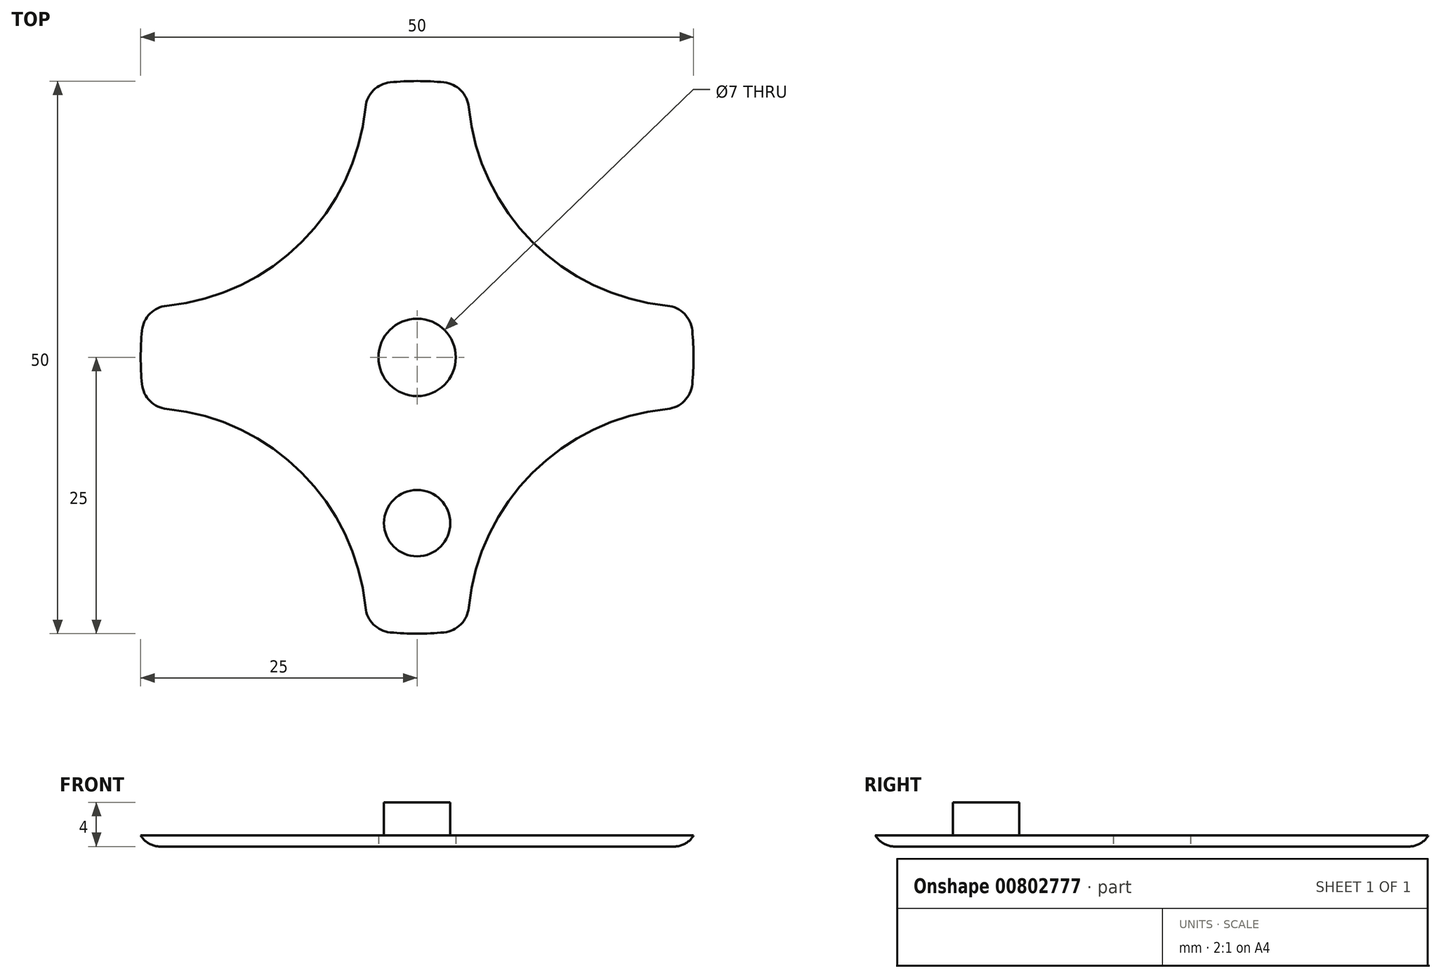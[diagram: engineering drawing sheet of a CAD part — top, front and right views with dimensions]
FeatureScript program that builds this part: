
annotation { "Feature Type Name" : "Feature", "Feature Type Description" : "" }
export const myFeature = defineFeature(function(context is Context, id is Id, definition is map)
    precondition{}
    {
        {
            var Q0;
            Q0=qCreatedBy(makeId("Top.planeOp"),FACE);
            var sketch = newSketch(context, id + "F0", { "sketchPlane" : qUnion([Q0])});
            skPoint(sketch, "E0.middle", {"position": v(0, 0) * mm});
            skArc(sketch, "E1", {"start": v(-24.58, 4.58) * mm, "mid": v(-25, 0) * mm, "end": v(-24.58, -4.58) * mm});
            skArc(sketch, "E2", {"start": v(-24.58, 4.58) * mm, "mid": v(-10.44, 10.44) * mm, "end": v(-4.58, 24.58) * mm});
            skLineSegment(sketch, "E3", {"start": v(0, 0) * mm, "end": v(-22.22, 22.22) * mm, "construction": true});
            skLineSegment(sketch, "E4", {"start": v(-4.58, 85.03) * mm, "end": v(-4.58, 7.7) * mm});
            skArc(sketch, "E5.1.0", {"start": v(-4.58, -24.58) * mm, "mid": v(-10.44, -10.44) * mm, "end": v(-24.58, -4.58) * mm});
            skArc(sketch, "E5.2.0", {"start": v(24.58, -4.58) * mm, "mid": v(10.44, -10.44) * mm, "end": v(4.58, -24.58) * mm});
            skArc(sketch, "E5.3.0", {"start": v(4.58, 24.58) * mm, "mid": v(10.44, 10.44) * mm, "end": v(24.58, 4.58) * mm});
            skArc(sketch, "E6.trimOffspring", {"start": v(4.58, 24.58) * mm, "mid": v(0, 25) * mm, "end": v(-4.58, 24.58) * mm});
            skArc(sketch, "E7.trimOffspring", {"start": v(24.58, -4.58) * mm, "mid": v(25, 0) * mm, "end": v(24.58, 4.58) * mm});
            skArc(sketch, "E8.trimOffspring", {"start": v(-4.58, -24.58) * mm, "mid": v(0, -25) * mm, "end": v(4.58, -24.58) * mm});
            skCircle(sketch, "E9", {"center": v(0, 0) * mm, "radius": 3.5 * mm});
            skSolve(sketch);
        }
        {
            var Q0;
            Q0=makeQuery(id+"F0.imprint","IMPRINT",FACE,{"disambiguationData":[TD([[makeQuery(id+"F0.imprint","IMPRINT",EDGE,{"derivedFrom":sQuery(id+"F0.wireOp",EDGE,"E0.bottom")}),1.0]])]});
            var Q1;
            Q1=makeQuery(id+"F0.imprint","IMPRINT",FACE,{"disambiguationData":[TD([[makeQuery(id+"F0.imprint","IMPRINT",EDGE,{"derivedFrom":sQuery(id+"F0.wireOp",EDGE,"E1")}),1.0]])]});
            extrude(context, id + "F1", {"entities" : qUnion([Q0, Q1]), "depth" : 4 * mm, "offsetDistance" : 25 * mm});
        }
        {
            var Q0;
            Q0=makeQuery(id+"F1.opExtrude","SWEPT_EDGE",EDGE,{"disambiguationData":[OSD([sQuery(id+"F0.wireOp",EDGE,"E5.1.0"),sQuery(id+"F0.wireOp",EDGE,"E8.trimOffspring")])]});
            var Q1;
            Q1=makeQuery(id+"F1.opExtrude","SWEPT_EDGE",EDGE,{"disambiguationData":[OSD([sQuery(id+"F0.wireOp",EDGE,"E1"),sQuery(id+"F0.wireOp",EDGE,"E5.1.0")])]});
            var Q2;
            Q2=makeQuery(id+"F1.opExtrude","SWEPT_EDGE",EDGE,{"disambiguationData":[OSD([sQuery(id+"F0.wireOp",EDGE,"E5.2.0"),sQuery(id+"F0.wireOp",EDGE,"E8.trimOffspring")])]});
            var Q3;
            Q3=makeQuery(id+"F1.opExtrude","SWEPT_EDGE",EDGE,{"disambiguationData":[OSD([sQuery(id+"F0.wireOp",EDGE,"E5.2.0"),sQuery(id+"F0.wireOp",EDGE,"E7.trimOffspring")])]});
            var Q4;
            Q4=makeQuery(id+"F1.opExtrude","SWEPT_EDGE",EDGE,{"disambiguationData":[OSD([sQuery(id+"F0.wireOp",EDGE,"E1"),sQuery(id+"F0.wireOp",EDGE,"E2")])]});
            var Q5;
            Q5=makeQuery(id+"F1.opExtrude","SWEPT_EDGE",EDGE,{"disambiguationData":[OSD([sQuery(id+"F0.wireOp",EDGE,"E2"),sQuery(id+"F0.wireOp",EDGE,"E6.trimOffspring")])]});
            var Q6;
            Q6=makeQuery(id+"F1.opExtrude","SWEPT_EDGE",EDGE,{"disambiguationData":[OSD([sQuery(id+"F0.wireOp",EDGE,"E5.3.0"),sQuery(id+"F0.wireOp",EDGE,"E6.trimOffspring")])]});
            var Q7;
            Q7=makeQuery(id+"F1.opExtrude","SWEPT_EDGE",EDGE,{"disambiguationData":[OSD([sQuery(id+"F0.wireOp",EDGE,"E5.3.0"),sQuery(id+"F0.wireOp",EDGE,"E7.trimOffspring")])]});
            fillet(context, id + "F2", {"entities" : qUnion([Q0, Q1, Q2, Q3, Q4, Q5, Q6, Q7]), "radius" : 2.5 * mm, "tangentPropagation" : true, "allowEdgeOverflow" : false});
        }
        {
            var Q0;
            Q0=makeQuery(id+"F1.opExtrude","CAP_FACE",FACE,{"disambiguationData":[OSD([sQuery(id+"F0.wireOp",EDGE,"E0.bottom"),sQuery(id+"F0.wireOp",EDGE,"E0.top"),sQuery(id+"F0.wireOp",EDGE,"E0.left"),sQuery(id+"F0.wireOp",EDGE,"E0.right"),sQuery(id+"F0.wireOp",EDGE,"E1"),sQuery(id+"F0.wireOp",EDGE,"E2"),sQuery(id+"F0.wireOp",EDGE,"E5.1.0"),sQuery(id+"F0.wireOp",EDGE,"E5.2.0"),sQuery(id+"F0.wireOp",EDGE,"E5.3.0"),sQuery(id+"F0.wireOp",EDGE,"E6.trimOffspring"),sQuery(id+"F0.wireOp",EDGE,"E7.trimOffspring"),sQuery(id+"F0.wireOp",EDGE,"E8.trimOffspring")])],"isStart":false});
            var sketch = newSketch(context, id + "F3", { "sketchPlane" : qUnion([Q0])});
            skCircle(sketch, "E10", {"center": v(0, 15) * mm, "radius": 3 * mm});
            skCircle(sketch, "E11.MirrorC", {"center": v(0, -15) * mm, "radius": 3 * mm});
            skSolve(sketch);
        }
        {
            var Q0;
            Q0=makeQuery(id+"F3.imprint","IMPRINT",FACE,{"disambiguationData":[TD([[makeQuery(id+"F3.imprint","IMPRINT",EDGE,{"derivedFrom":sQuery(id+"F3.wireOp",EDGE,"E10")}),1.0]])]});
            var Q1;
            Q1=makeQuery(id+"F3.imprint","IMPRINT",FACE,{"disambiguationData":[TD([[makeQuery(id+"F3.imprint","IMPRINT",EDGE,{"derivedFrom":sQuery(id+"F3.wireOp",EDGE,"E11.MirrorC")}),-1.0]])]});
            extrude(context, id + "F4", {"entities" : qUnion([Q0, Q1]), "operationType" : NewBodyOperationType.REMOVE, "oppositeDirection" : true, "depth" : 3 * mm, "offsetDistance" : 25 * mm});
        }
        {
            var Q0;
            Q0=makeQuery(id+"F1.opExtrude","CAP_EDGE",EDGE,{"disambiguationData":[OSD([sQuery(id+"F0.wireOp",EDGE,"E5.3.0")])],"isStart":true});
            fillet(context, id + "F5", {"entities" : qUnion([Q0]), "radius" : 2 * mm, "tangentPropagation" : true, "allowEdgeOverflow" : false});
        }
    });
